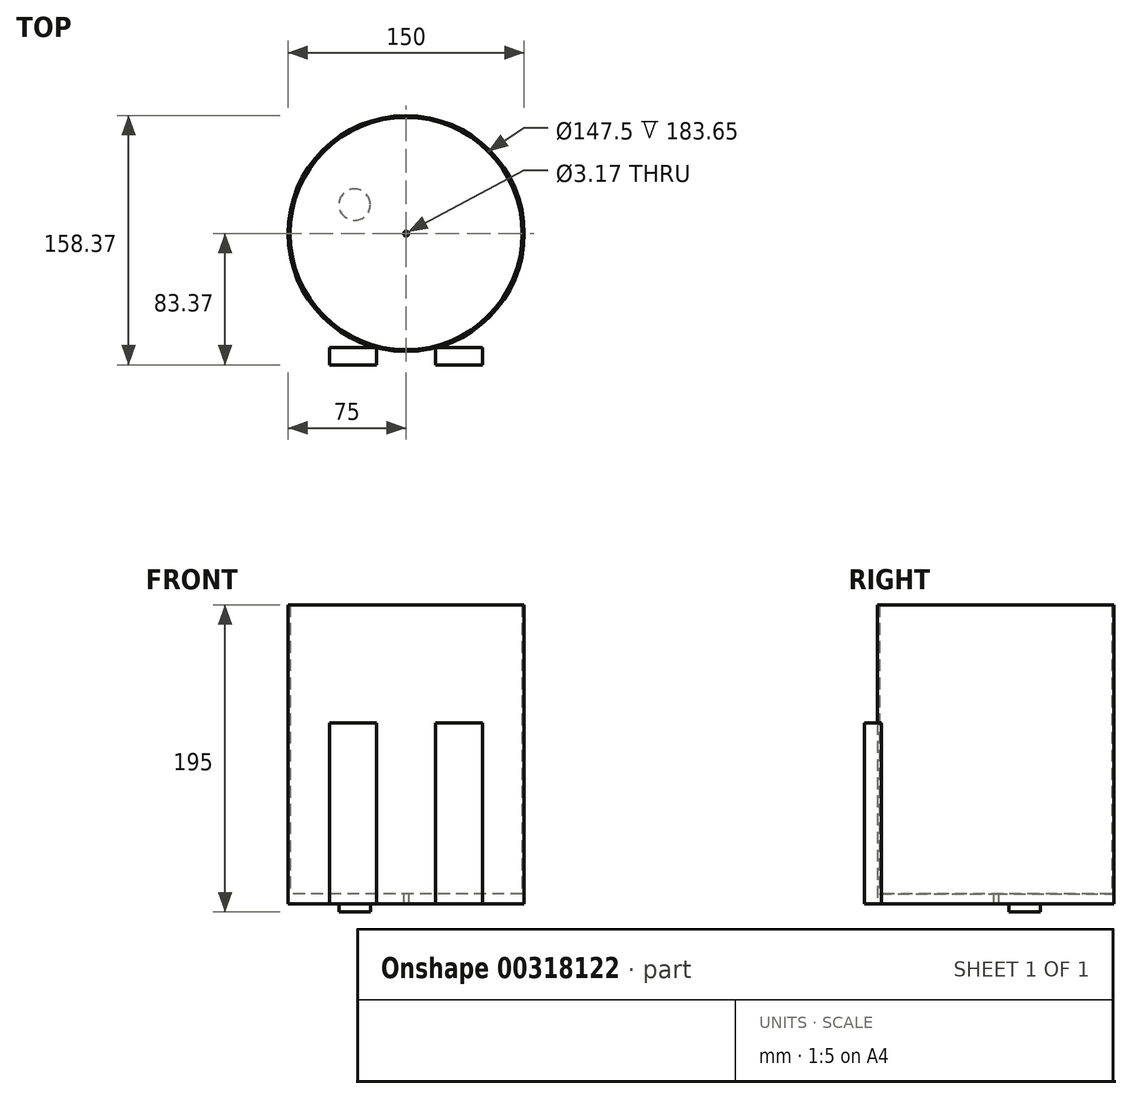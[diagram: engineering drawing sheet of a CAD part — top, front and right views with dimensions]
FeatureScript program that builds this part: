
annotation { "Feature Type Name" : "Feature", "Feature Type Description" : "" }
export const myFeature = defineFeature(function(context is Context, id is Id, definition is map)
    precondition{}
    {
        {
            var Q0;
            Q0=qCreatedBy(makeId("Top.planeOp"),FACE);
            var sketch = newSketch(context, id + "F0", { "sketchPlane" : qUnion([Q0])});
            skCircle(sketch, "E0", {"center": v(0, 0) * mm, "radius": 75 * mm});
            skCircle(sketch, "E1", {"center": v(0, 0) * mm, "radius": 73.75 * mm});
            skSolve(sketch);
        }
        {
            var Q0;
            Q0=makeQuery(id+"F0.imprint","IMPRINT",FACE,{"disambiguationData":[TD([[makeQuery(id+"F0.imprint","IMPRINT",EDGE,{"derivedFrom":sQuery(id+"F0.wireOp",EDGE,"E0")}),1.0]])]});
            var sketch = newSketch(context, id + "F1", { "sketchPlane" : qUnion([Q0])});
            skLineSegment(sketch, "E2", {"start": v(0, -84.76) * mm, "end": v(0, -52.66) * mm, "construction": true});
            skPoint(sketch, "E3.start.orphan", {"position": v(0, -75.17) * mm});
            skPoint(sketch, "E4.end.orphan", {"position": v(18.66, -79.94) * mm});
            skLineSegment(sketch, "E5", {"start": v(18.66, -83.37) * mm, "end": v(48.66, -83.37) * mm});
            skPoint(sketch, "E6.orphan", {"position": v(18.66, -72.5) * mm});
            skPoint(sketch, "E7.start.orphan", {"position": v(48.66, -73.37) * mm});
            skLineSegment(sketch, "E8.MirrorCS", {"start": v(-18.66, -83.37) * mm, "end": v(-48.66, -83.37) * mm});
            skPoint(sketch, "E9.MirrorP", {"position": v(-18.66, -72.5) * mm});
            skPoint(sketch, "E10.MirrorP", {"position": v(-18.66, -79.94) * mm});
            skPoint(sketch, "E11.MirrorP", {"position": v(-48.66, -73.37) * mm});
            skPoint(sketch, "E12.MirrorCS.end.orphan", {"position": v(-18.66, -83.37) * mm});
            skPoint(sketch, "E12.MirrorCS.start.orphan", {"position": v(-18.66, -73.37) * mm});
            skPoint(sketch, "E13.MirrorCS.end.orphan", {"position": v(-48.66, -83.37) * mm});
            skLineSegment(sketch, "E14", {"start": v(-48.66, -83.37) * mm, "end": v(-48.66, -72.5) * mm});
            skLineSegment(sketch, "E15", {"start": v(-48.66, -72.5) * mm, "end": v(-18.66, -72.5) * mm});
            skLineSegment(sketch, "E16", {"start": v(-18.66, -72.5) * mm, "end": v(-18.66, -83.37) * mm});
            skPoint(sketch, "E17.start.orphan", {"position": v(18.66, -73.37) * mm});
            skLineSegment(sketch, "E18.MirrorCS", {"start": v(48.66, -72.5) * mm, "end": v(18.66, -72.5) * mm});
            skLineSegment(sketch, "E19.MirrorCS", {"start": v(18.66, -72.5) * mm, "end": v(18.66, -83.37) * mm});
            skLineSegment(sketch, "E20.MirrorCS", {"start": v(48.66, -83.37) * mm, "end": v(48.66, -72.5) * mm});
            skSolve(sketch);
        }
        {
            var Q0;
            Q0 = qSketchRegion(id + "F1", true);
            extrude(context, id + "F2", {"entities" : qUnion([Q0]), "depth" : 115 * mm});
        }
        {
            var Q0;
            Q0 = qSketchRegion(id + "F0", true);
            extrude(context, id + "F3", {"entities" : qUnion([Q0]), "depth" : 190 * mm});
        }
        {
            var Q0;
            Q0=makeQuery(id+"F0.imprint","IMPRINT",FACE,{"disambiguationData":[TD([[makeQuery(id+"F0.imprint","IMPRINT",EDGE,{"derivedFrom":sQuery(id+"F0.wireOp",EDGE,"E1")}),1.0]])]});
            extrude(context, id + "F4", {"entities" : qUnion([Q0]), "operationType" : NewBodyOperationType.ADD, "depth" : 6.35 * mm});
        }
        {
            var Q0;
            {var subQ0=sQuery(id+"F0.wireOp",EDGE,"E1");Q0=makeQuery(id+"F4.boolean.opBoolean","MERGE",FACE,{"derivedFrom":[makeQuery(id+"F3.opExtrude","CAP_FACE",FACE,{"disambiguationData":[OSD([sQuery(id+"F0.wireOp",EDGE,"E0"),subQ0])],"isStart":true}),makeQuery(id+"F4.opExtrude","CAP_FACE",FACE,{"disambiguationData":[OSD([subQ0])],"isStart":true})]});}
            var sketch = newSketch(context, id + "F5", { "sketchPlane" : qUnion([Q0])});
            skCircle(sketch, "E21", {"center": v(0, 0) * mm, "radius": 1.59 * mm});
            skCircle(sketch, "E22", {"center": v(-32.7, -18.4) * mm, "radius": 10 * mm});
            skSolve(sketch);
        }
        {
            var Q0;
            Q0=makeQuery(id+"F5.imprint","IMPRINT",FACE,{"disambiguationData":[TD([[makeQuery(id+"F5.imprint","IMPRINT",EDGE,{"derivedFrom":sQuery(id+"F5.wireOp",EDGE,"E21")}),1.0]])]});
            extrude(context, id + "F6", {"entities" : qUnion([Q0]), "operationType" : NewBodyOperationType.REMOVE, "endBound" : BoundingType.THROUGH_ALL, "oppositeDirection" : true, "depth" : 25.4 * mm});
        }
        {
            var Q0;
            Q0=makeQuery(id+"F5.imprint","IMPRINT",FACE,{"disambiguationData":[TD([[makeQuery(id+"F5.imprint","IMPRINT",EDGE,{"derivedFrom":sQuery(id+"F5.wireOp",EDGE,"E22")}),1.0]])]});
            extrude(context, id + "F7", {"entities" : qUnion([Q0]), "operationType" : NewBodyOperationType.ADD, "depth" : 5 * mm});
        }
    });
